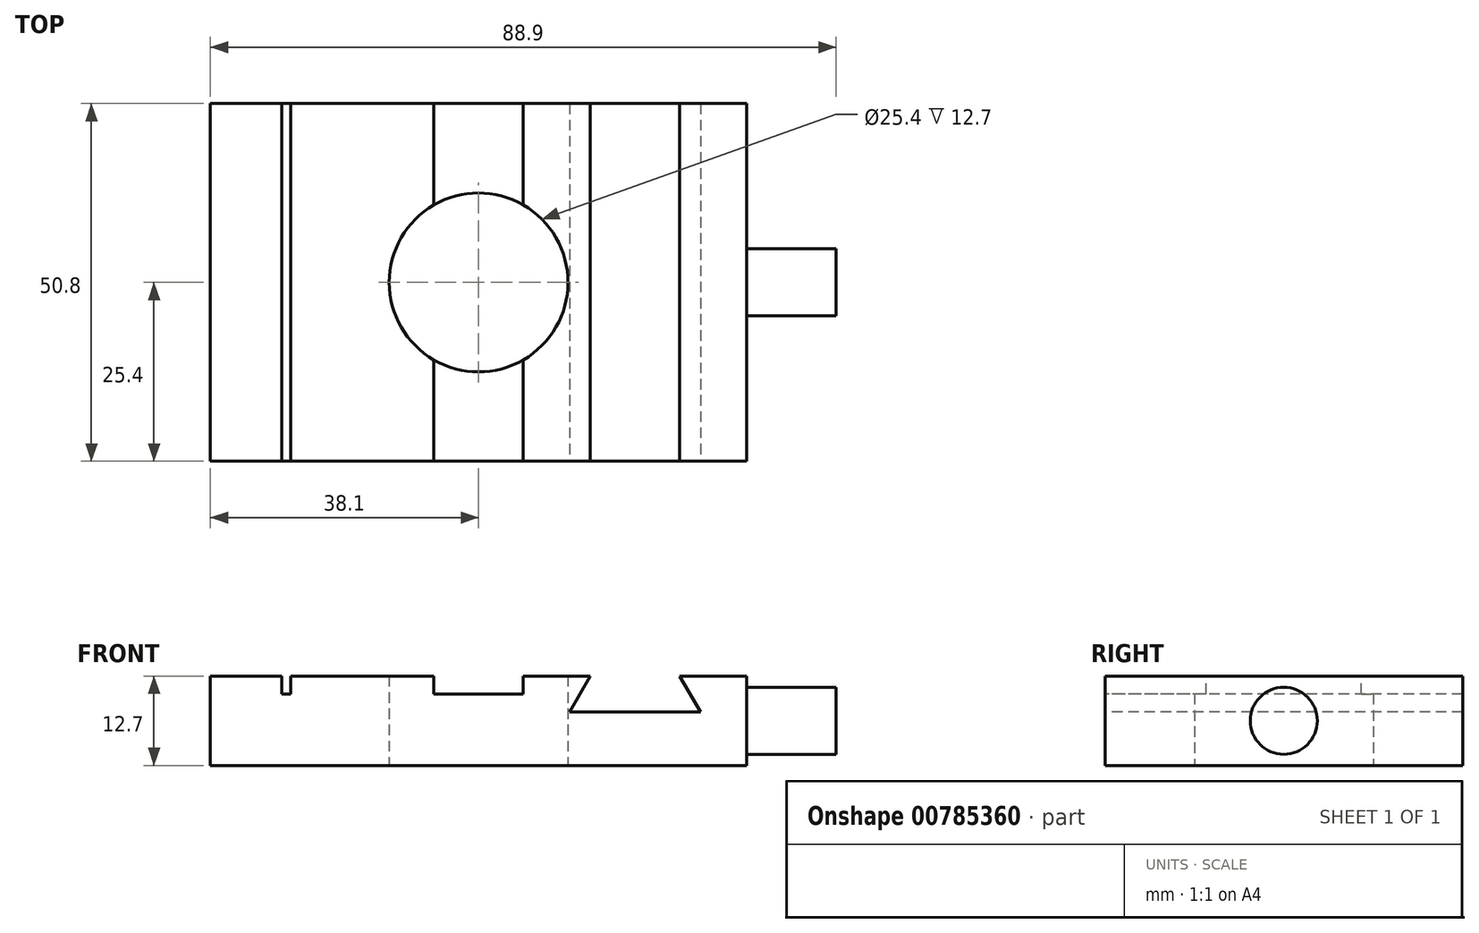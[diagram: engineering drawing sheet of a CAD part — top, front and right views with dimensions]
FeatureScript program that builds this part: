
annotation { "Feature Type Name" : "Feature", "Feature Type Description" : "" }
export const myFeature = defineFeature(function(context is Context, id is Id, definition is map)
    precondition{}
    {
        {
            var Q0;
            Q0=qCreatedBy(makeId("Top.planeOp"),FACE);
            var sketch = newSketch(context, id + "F0", { "sketchPlane" : qUnion([Q0])});
            skLineSegment(sketch, "E0.bottom", {"start": v(38.1, 25.4) * mm, "end": v(-38.1, 25.4) * mm});
            skLineSegment(sketch, "E0.top", {"start": v(38.1, -25.4) * mm, "end": v(-38.1, -25.4) * mm});
            skLineSegment(sketch, "E0.left", {"start": v(38.1, 25.4) * mm, "end": v(38.1, -25.4) * mm});
            skLineSegment(sketch, "E0.right", {"start": v(-38.1, 25.4) * mm, "end": v(-38.1, -25.4) * mm});
            skPoint(sketch, "E0.middle", {"position": v(0, 0) * mm});
            skCircle(sketch, "E1", {"center": v(0, 0) * mm, "radius": 12.7 * mm});
            skSolve(sketch);
        }
        {
            var Q0;
            Q0=makeQuery(id+"F0.imprint","IMPRINT",FACE,{"disambiguationData":[TD([[makeQuery(id+"F0.imprint","IMPRINT",EDGE,{"derivedFrom":sQuery(id+"F0.wireOp",EDGE,"E0.bottom")}),1.0]])]});
            extrude(context, id + "F1", {"entities" : qUnion([Q0]), "depth" : 12.7 * mm, "offsetDistance" : 25.4 * mm});
        }
        {
            var Q0;
            Q0=makeQuery(id+"F1.opExtrude","CAP_FACE",FACE,{"disambiguationData":[OSD([sQuery(id+"F0.wireOp",EDGE,"E0.bottom"),sQuery(id+"F0.wireOp",EDGE,"E0.top"),sQuery(id+"F0.wireOp",EDGE,"E0.left"),sQuery(id+"F0.wireOp",EDGE,"E0.right"),sQuery(id+"F0.wireOp",EDGE,"E1")])],"isStart":false});
            var sketch = newSketch(context, id + "F2", { "sketchPlane" : qUnion([Q0])});
            skLineSegment(sketch, "E2.bottom", {"start": v(-27.94, 25.4) * mm, "end": v(-26.67, 25.4) * mm});
            skLineSegment(sketch, "E2.top", {"start": v(-27.94, -25.4) * mm, "end": v(-26.67, -25.4) * mm});
            skLineSegment(sketch, "E2.left", {"start": v(-27.94, 25.4) * mm, "end": v(-27.94, -25.4) * mm});
            skLineSegment(sketch, "E2.right", {"start": v(-26.67, 25.4) * mm, "end": v(-26.67, -25.4) * mm});
            skLineSegment(sketch, "E3", {"start": v(-6.35, 25.4) * mm, "end": v(-6.35, -25.4) * mm});
            skLineSegment(sketch, "E4", {"start": v(-6.35, -25.4) * mm, "end": v(6.35, -25.4) * mm});
            skLineSegment(sketch, "E5", {"start": v(6.35, -25.4) * mm, "end": v(6.35, 25.4) * mm});
            skLineSegment(sketch, "E6", {"start": v(6.35, 25.4) * mm, "end": v(-6.35, 25.4) * mm});
            skPoint(sketch, "E7", {"position": v(0, 0) * mm});
            skLineSegment(sketch, "E8", {"start": v(0, -25.4) * mm, "end": v(0, 25.4) * mm, "construction": true});
            skSolve(sketch);
        }
        {
            var Q0;
            Q0=makeQuery(id+"F2.imprint","IMPRINT",FACE,{"disambiguationData":[TD([[makeQuery(id+"F2.imprint","IMPRINT",EDGE,{"derivedFrom":sQuery(id+"F2.wireOp",EDGE,"E2.bottom")}),1.0]])]});
            var Q1;
            {var subQ0=sQuery(id+"F2.wireOp",EDGE,"E4");Q1=makeQuery(id+"F2.imprint","IMPRINT",FACE,{"disambiguationData":[TD([[makeQuery(id+"F2.imprint","IMPRINT",EDGE,{"derivedFrom":subQ0}),-1.0]])]});}
            var Q2;
            {var subQ0=sQuery(id+"F2.wireOp",EDGE,"E6");Q2=makeQuery(id+"F2.imprint","IMPRINT",FACE,{"disambiguationData":[TD([[makeQuery(id+"F2.imprint","IMPRINT",EDGE,{"derivedFrom":subQ0}),1.0]])]});}
            extrude(context, id + "F3", {"entities" : qUnion([Q0, Q1, Q2]), "operationType" : NewBodyOperationType.REMOVE, "oppositeDirection" : true, "depth" : 2.54 * mm, "offsetDistance" : 25.4 * mm});
        }
        {
            var Q0;
            Q0=makeQuery(id+"F1.opExtrude","SWEPT_FACE",FACE,{"disambiguationData":[OSD([sQuery(id+"F0.wireOp",EDGE,"E0.top")])]});
            var sketch = newSketch(context, id + "F4", { "sketchPlane" : qUnion([Q0])});
            skLineSegment(sketch, "E9", {"start": v(15.88, 12.7) * mm, "end": v(12.94, 7.62) * mm});
            skLineSegment(sketch, "E10", {"start": v(12.94, 7.62) * mm, "end": v(31.5, 7.62) * mm});
            skLineSegment(sketch, "E11", {"start": v(31.5, 7.62) * mm, "end": v(28.57, 12.7) * mm});
            skLineSegment(sketch, "E12", {"start": v(28.57, 12.7) * mm, "end": v(15.88, 12.7) * mm});
            skLineSegment(sketch, "E13", {"start": v(22.23, 7.62) * mm, "end": v(22.23, 12.7) * mm, "construction": true});
            skPoint(sketch, "E14", {"position": v(22.23, 12.7) * mm});
            skSolve(sketch);
        }
        {
            var Q0;
            Q0=makeQuery(id+"F4.imprint","IMPRINT",FACE,{"disambiguationData":[TD([[makeQuery(id+"F4.imprint","IMPRINT",EDGE,{"derivedFrom":sQuery(id+"F4.wireOp",EDGE,"E9")}),1.0]])]});
            extrude(context, id + "F5", {"entities" : qUnion([Q0]), "operationType" : NewBodyOperationType.REMOVE, "oppositeDirection" : true, "depth" : 50.8 * mm, "offsetDistance" : 25.4 * mm});
        }
        {
            var Q0;
            Q0=makeQuery(id+"F1.opExtrude","SWEPT_FACE",FACE,{"disambiguationData":[OSD([sQuery(id+"F0.wireOp",EDGE,"E0.left")])]});
            var sketch = newSketch(context, id + "F6", { "sketchPlane" : qUnion([Q0])});
            skCircle(sketch, "E15", {"center": v(0, 6.35) * mm, "radius": 4.76 * mm});
            skPoint(sketch, "E15.centerSnap0", {"position": v(-25.4, 6.35) * mm});
            skPoint(sketch, "E15.centerSnap1", {"position": v(0, 12.7) * mm});
            skSolve(sketch);
        }
        {
            var Q0;
            Q0=makeQuery(id+"F6.imprint","IMPRINT",FACE,{"disambiguationData":[TD([[makeQuery(id+"F6.imprint","IMPRINT",EDGE,{"derivedFrom":sQuery(id+"F6.wireOp",EDGE,"E15")}),1.0]])]});
            extrude(context, id + "F7", {"entities" : qUnion([Q0]), "operationType" : NewBodyOperationType.ADD, "depth" : 12.7 * mm, "offsetDistance" : 25.4 * mm});
        }
    });
